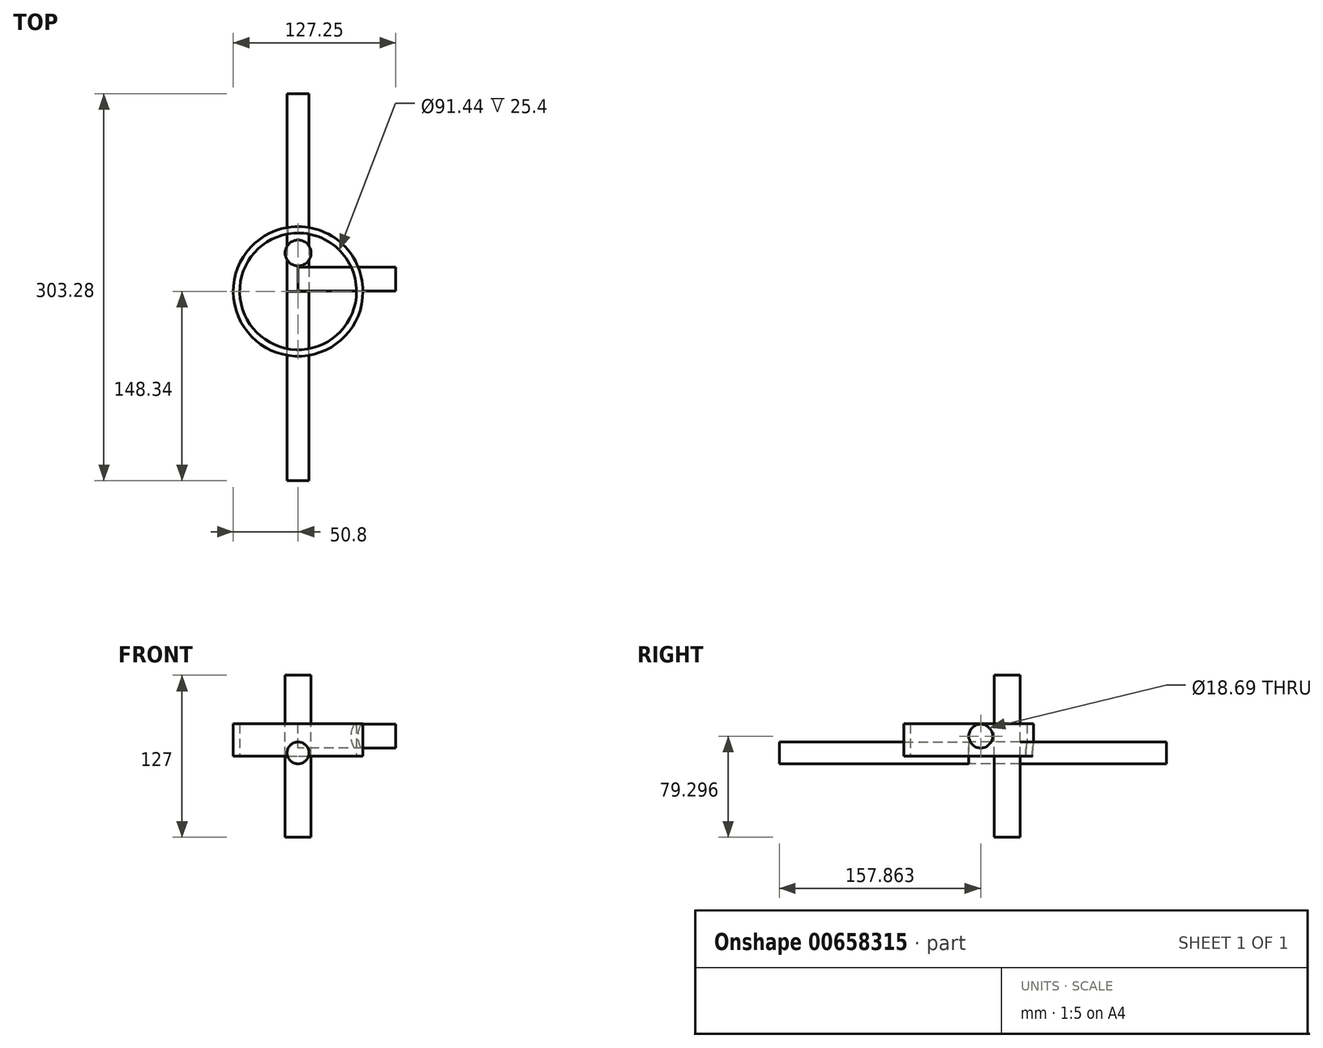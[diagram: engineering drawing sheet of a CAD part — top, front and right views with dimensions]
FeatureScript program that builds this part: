
annotation { "Feature Type Name" : "Feature", "Feature Type Description" : "" }
export const myFeature = defineFeature(function(context is Context, id is Id, definition is map)
    precondition{}
    {
        {
            var Q0;
            Q0=qCreatedBy(makeId("Top.planeOp"),FACE);
            var sketch = newSketch(context, id + "F0", { "sketchPlane" : qUnion([Q0])});
            skCircle(sketch, "E0", {"center": v(0, 0) * mm, "radius": 50.8 * mm});
            skSolve(sketch);
        }
        {
            var Q0;
            Q0=makeQuery(id+"F0.imprint","IMPRINT",FACE,{"disambiguationData":[TD([[makeQuery(id+"F0.imprint","IMPRINT",EDGE,{"derivedFrom":sQuery(id+"F0.wireOp",EDGE,"E0")}),1.0]])]});
            extrude(context, id + "F1", {"entities" : qUnion([Q0]), "depth" : 25.4 * mm, "offsetDistance" : 25.4 * mm});
        }
        {
            var Q0;
            Q0=makeQuery(id+"F1.opExtrude","CAP_FACE",FACE,{"disambiguationData":[OSD([sQuery(id+"F0.wireOp",EDGE,"E0")])],"isStart":false});
            var Q1;
            Q1=makeQuery(id+"F1.opExtrude","CAP_FACE",FACE,{"disambiguationData":[OSD([sQuery(id+"F0.wireOp",EDGE,"E0")])],"isStart":true});
            shell(context, id + "F2", {"entities" : qUnion([Q0, Q1]), "thickness" : 5.08 * mm});
        }
        {
            var Q0;
            Q0=qCreatedBy(makeId("Front.planeOp"),FACE);
            var sketch = newSketch(context, id + "F3", { "sketchPlane" : qUnion([Q0])});
            skCircle(sketch, "E1", {"center": v(0, 2.66) * mm, "radius": 8.57 * mm});
            skSolve(sketch);
        }
        {
            var Q0;
            Q0 = qSketchRegion(id + "F3", true);
            extrude(context, id + "F4", {"entities" : qUnion([Q0]), "depth" : 148.34 * mm, "offsetDistance" : 25.4 * mm});
        }
        {
            var Q0;
            Q0=makeQuery(id+"F3.imprint","IMPRINT",FACE,{"disambiguationData":[TD([[makeQuery(id+"F3.imprint","IMPRINT",EDGE,{"derivedFrom":sQuery(id+"F3.wireOp",EDGE,"E1")}),1.0]])]});
            extrude(context, id + "F5", {"entities" : qUnion([Q0]), "oppositeDirection" : true, "depth" : 154.94 * mm, "offsetDistance" : 25.4 * mm});
        }
        {
            var Q0;
            Q0=qCreatedBy(makeId("Top.planeOp"),FACE);
            var sketch = newSketch(context, id + "F6", { "sketchPlane" : qUnion([Q0])});
            skCircle(sketch, "E2", {"center": v(0, 30.11) * mm, "radius": 10.17 * mm});
            skSolve(sketch);
        }
        {
            var Q0;
            Q0 = qSketchRegion(id + "F6", true);
            extrude(context, id + "F7", {"entities" : qUnion([Q0]), "endBound" : BoundingType.SYMMETRIC, "oppositeDirection" : true, "depth" : 127 * mm, "offsetDistance" : 25.4 * mm});
        }
        {
            var Q0;
            Q0=qCreatedBy(makeId("Right.planeOp"),FACE);
            var sketch = newSketch(context, id + "F8", { "sketchPlane" : qUnion([Q0])});
            skCircle(sketch, "E3", {"center": v(9.52, 15.8) * mm, "radius": 9.35 * mm});
            skSolve(sketch);
        }
        {
            var Q0;
            Q0 = qSketchRegion(id + "F8", true);
            extrude(context, id + "F9", {"entities" : qUnion([Q0]), "depth" : 76.45 * mm, "offsetDistance" : 25.4 * mm});
        }
        {
            var Q0;
            Q0=makeQuery(id+"F5.opExtrude","SWEPT_BODY",BODY,{"disambiguationData":[OSD([sQuery(id+"F3.wireOp",EDGE,"E1")])]});
            var Q1;
            Q1=makeQuery(id+"F1.opExtrude","SWEPT_BODY",BODY,{"disambiguationData":[OSD([sQuery(id+"F0.wireOp",EDGE,"E0")])]});
            booleanBodies(context, id + "F10", {"operationType" : BooleanOperationType.SUBTRACTION, "tools" : qUnion([Q0]), "targets" : qUnion([Q1]), "keepTools" : true});
        }
        {
            var Q0;
            Q0=makeQuery(id+"F9.opExtrude","SWEPT_BODY",BODY,{"disambiguationData":[OSD([sQuery(id+"F8.wireOp",EDGE,"E3")])]});
            var Q1;
            Q1=makeQuery(id+"F1.opExtrude","SWEPT_BODY",BODY,{"disambiguationData":[OSD([sQuery(id+"F0.wireOp",EDGE,"E0")])]});
            booleanBodies(context, id + "F11", {"operationType" : BooleanOperationType.SUBTRACTION, "tools" : qUnion([Q0]), "targets" : qUnion([Q1]), "keepTools" : true});
        }
    });
